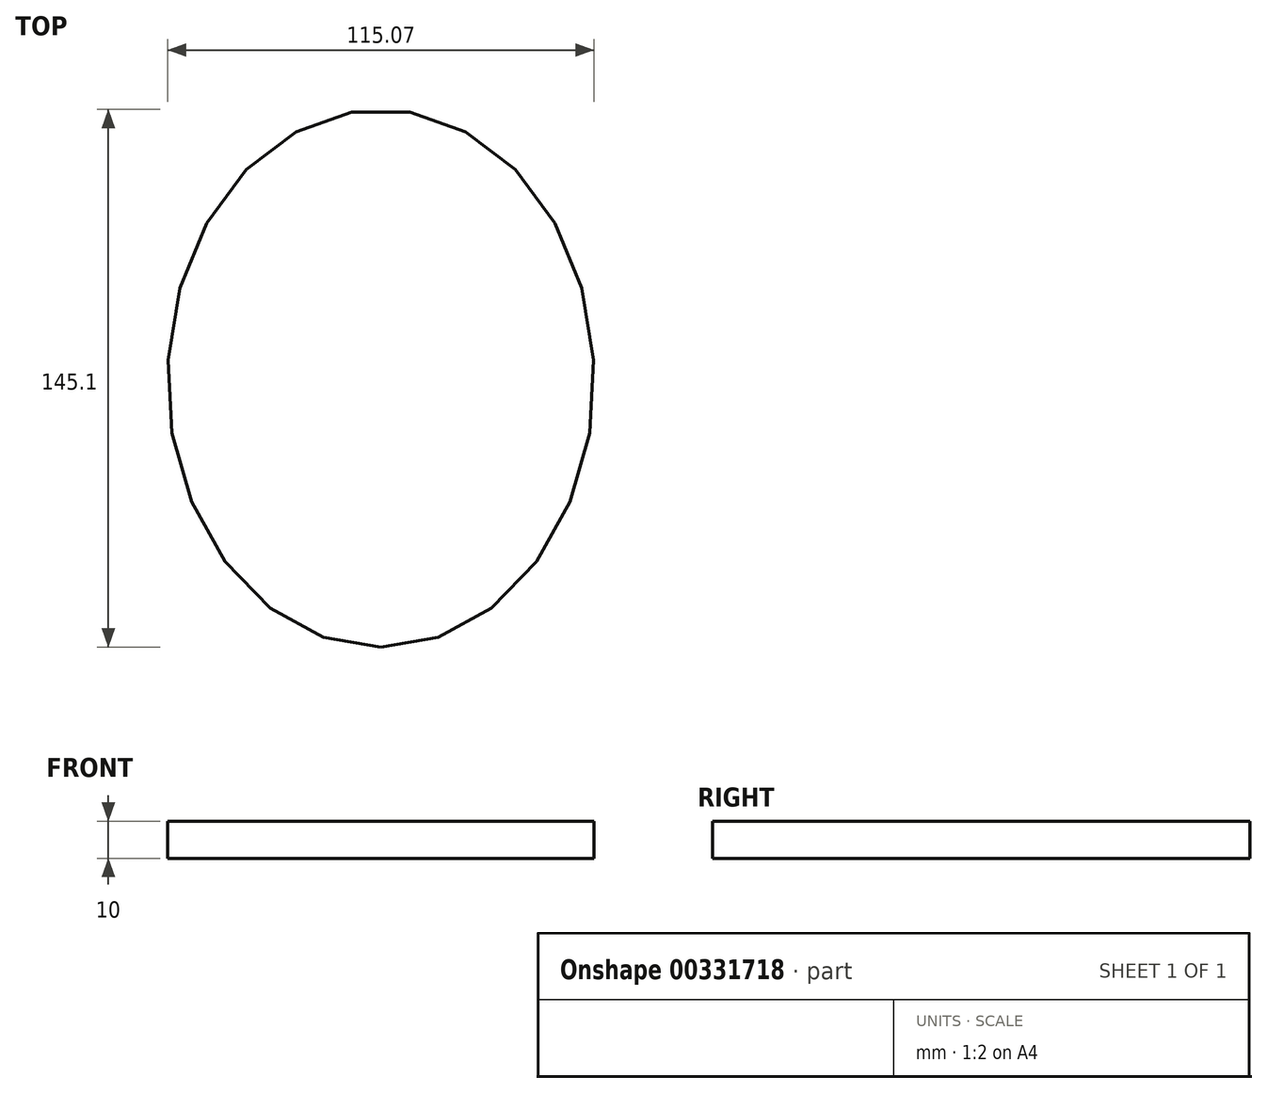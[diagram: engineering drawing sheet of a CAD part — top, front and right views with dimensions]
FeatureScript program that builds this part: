
annotation { "Feature Type Name" : "Feature", "Feature Type Description" : "" }
export const myFeature = defineFeature(function(context is Context, id is Id, definition is map)
    precondition{}
    {
        {
            var Q0;
            Q0=qCreatedBy(makeId("Top.planeOp"),FACE);
            var sketch = newSketch(context, id + "F0", { "sketchPlane" : qUnion([Q0])});
            skEllipse(sketch, "E0", {"center": v(51.81, 0) * mm, "majorRadius": 72.55 * mm, "minorRadius": 57.53 * mm, "majorAxis": v(0, -1)});
            skSolve(sketch);
        }
        {
            var Q0;
            Q0=makeQuery(id+"F0.imprint","IMPRINT",FACE,{"disambiguationData":[TD([[makeQuery(id+"F0.imprint","IMPRINT",EDGE,{"derivedFrom":sQuery(id+"F0.wireOp",EDGE,"E0")}),1.0]])]});
            extrude(context, id + "F1", {"entities" : qUnion([Q0]), "depth" : 10 * mm});
        }
    });
